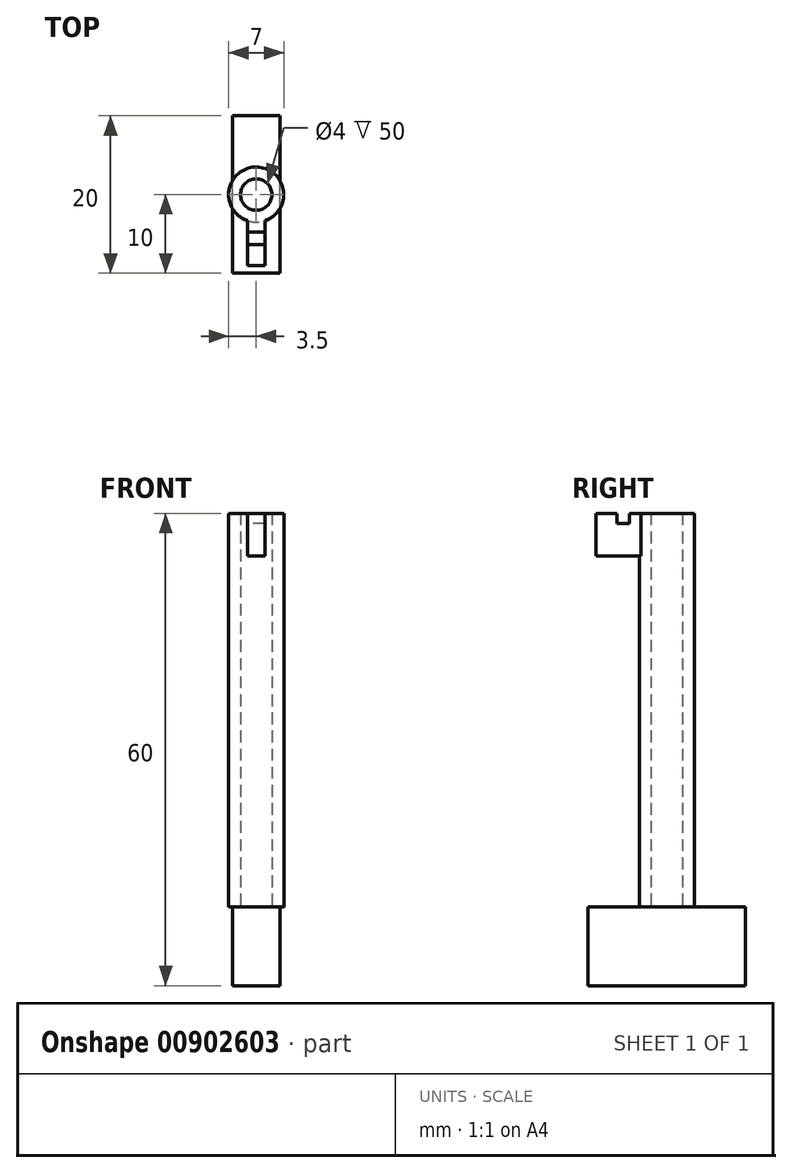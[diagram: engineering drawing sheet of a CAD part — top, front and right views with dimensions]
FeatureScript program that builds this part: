
annotation { "Feature Type Name" : "Feature", "Feature Type Description" : "" }
export const myFeature = defineFeature(function(context is Context, id is Id, definition is map)
    precondition{}
    {
        {
            var Q0;
            Q0=qCreatedBy(makeId("Top.planeOp"),FACE);
            var sketch = newSketch(context, id + "F0", { "sketchPlane" : qUnion([Q0])});
            skCircle(sketch, "E0", {"center": v(0, 0) * mm, "radius": 2 * mm});
            skCircle(sketch, "E1.0", {"center": v(0, 0) * mm, "radius": 3.5 * mm});
            skSolve(sketch);
        }
        {
            var Q0;
            Q0=makeQuery(id+"F0.imprint","IMPRINT",FACE,{"disambiguationData":[TD([[makeQuery(id+"F0.imprint","IMPRINT",EDGE,{"derivedFrom":sQuery(id+"F0.wireOp",EDGE,"E0")}),-1.0]])]});
            extrude(context, id + "F1", {"entities" : qUnion([Q0]), "depth" : 50 * mm, "offsetDistance" : 25 * mm});
        }
        {
            var Q0;
            Q0=qCreatedBy(makeId("Front.planeOp"),FACE);
            var sketch = newSketch(context, id + "F2", { "sketchPlane" : qUnion([Q0])});
            skLineSegment(sketch, "E2", {"start": v(-1.1, 50) * mm, "end": v(1.1, 50) * mm});
            skLineSegment(sketch, "E3", {"start": v(1.1, 50) * mm, "end": v(1.1, 44.57) * mm});
            skLineSegment(sketch, "E4", {"start": v(1.1, 44.57) * mm, "end": v(-1.1, 44.57) * mm});
            skLineSegment(sketch, "E5", {"start": v(-1.1, 44.57) * mm, "end": v(-1.1, 50) * mm});
            skPoint(sketch, "E6", {"position": v(0, 44.57) * mm});
            skSolve(sketch);
        }
        {
            var Q0;
            Q0 = qSketchRegion(id + "F2", true);
            extrude(context, id + "F3", {"entities" : qUnion([Q0]), "operationType" : NewBodyOperationType.ADD, "depth" : 9.02 * mm, "offsetDistance" : 25 * mm});
        }
        {
            var Q0;
            Q0 = qSketchRegion(id + "F2", true);
            var Q1;
            Q1=makeQuery(id+"F1.opExtrude","SWEPT_FACE",FACE,{"disambiguationData":[OSD([sQuery(id+"F0.wireOp",EDGE,"E0")])]});
            extrude(context, id + "F4", {"entities" : qUnion([Q0]), "operationType" : NewBodyOperationType.REMOVE, "endBound" : BoundingType.UP_TO_SURFACE, "depth" : 25 * mm, "endBoundEntityFace" : qUnion([Q1]), "offsetDistance" : 25 * mm});
        }
        {
            var Q0;
            Q0=makeQuery(id+"F3.boolean.opBoolean","MERGE",FACE,{"derivedFrom":[makeQuery(id+"F1.opExtrude","CAP_FACE",FACE,{"disambiguationData":[OSD([sQuery(id+"F0.wireOp",EDGE,"E0"),sQuery(id+"F0.wireOp",EDGE,"E1.0")])],"isStart":false}),makeQuery(id+"F3.opExtrude","SWEPT_FACE",FACE,{"disambiguationData":[OSD([sQuery(id+"F2.wireOp",EDGE,"E2")])]})]});
            var sketch = newSketch(context, id + "F5", { "sketchPlane" : qUnion([Q0])});
            skLineSegment(sketch, "E7", {"start": v(1.1, -6.37) * mm, "end": v(-1.1, -6.37) * mm});
            skLineSegment(sketch, "E8", {"start": v(-1.1, -6.37) * mm, "end": v(-1.1, -4.77) * mm});
            skLineSegment(sketch, "E9", {"start": v(-1.1, -4.77) * mm, "end": v(1.1, -4.77) * mm});
            skLineSegment(sketch, "E10", {"start": v(1.1, -4.77) * mm, "end": v(1.1, -6.37) * mm});
            skSolve(sketch);
        }
        {
            var Q0;
            Q0=makeQuery(id+"F5.imprint","IMPRINT",FACE,{"disambiguationData":[TD([[makeQuery(id+"F5.imprint","IMPRINT",EDGE,{"derivedFrom":sQuery(id+"F5.wireOp",EDGE,"E7")}),-1.0]])]});
            extrude(context, id + "F6", {"entities" : qUnion([Q0]), "operationType" : NewBodyOperationType.REMOVE, "oppositeDirection" : true, "depth" : 1.3 * mm, "offsetDistance" : 25 * mm});
        }
        {
            var Q0;
            Q0=makeQuery(id+"F1.opExtrude","CAP_FACE",FACE,{"disambiguationData":[OSD([sQuery(id+"F0.wireOp",EDGE,"E0"),sQuery(id+"F0.wireOp",EDGE,"E1.0")])],"isStart":true});
            var sketch = newSketch(context, id + "F7", { "sketchPlane" : qUnion([Q0])});
            skLineSegment(sketch, "E11.bottom", {"start": v(3, 10) * mm, "end": v(-3, 10) * mm});
            skLineSegment(sketch, "E11.top", {"start": v(3, -10) * mm, "end": v(-3, -10) * mm});
            skLineSegment(sketch, "E11.left", {"start": v(3, 10) * mm, "end": v(3, -10) * mm});
            skLineSegment(sketch, "E11.right", {"start": v(-3, 10) * mm, "end": v(-3, -10) * mm});
            skPoint(sketch, "E11.middle", {"position": v(0, 0) * mm});
            skSolve(sketch);
        }
        {
            var Q0;
            Q0 = qSketchRegion(id + "F7", true);
            extrude(context, id + "F8", {"entities" : qUnion([Q0]), "operationType" : NewBodyOperationType.ADD, "depth" : 10 * mm, "offsetDistance" : 25 * mm});
        }
    });
